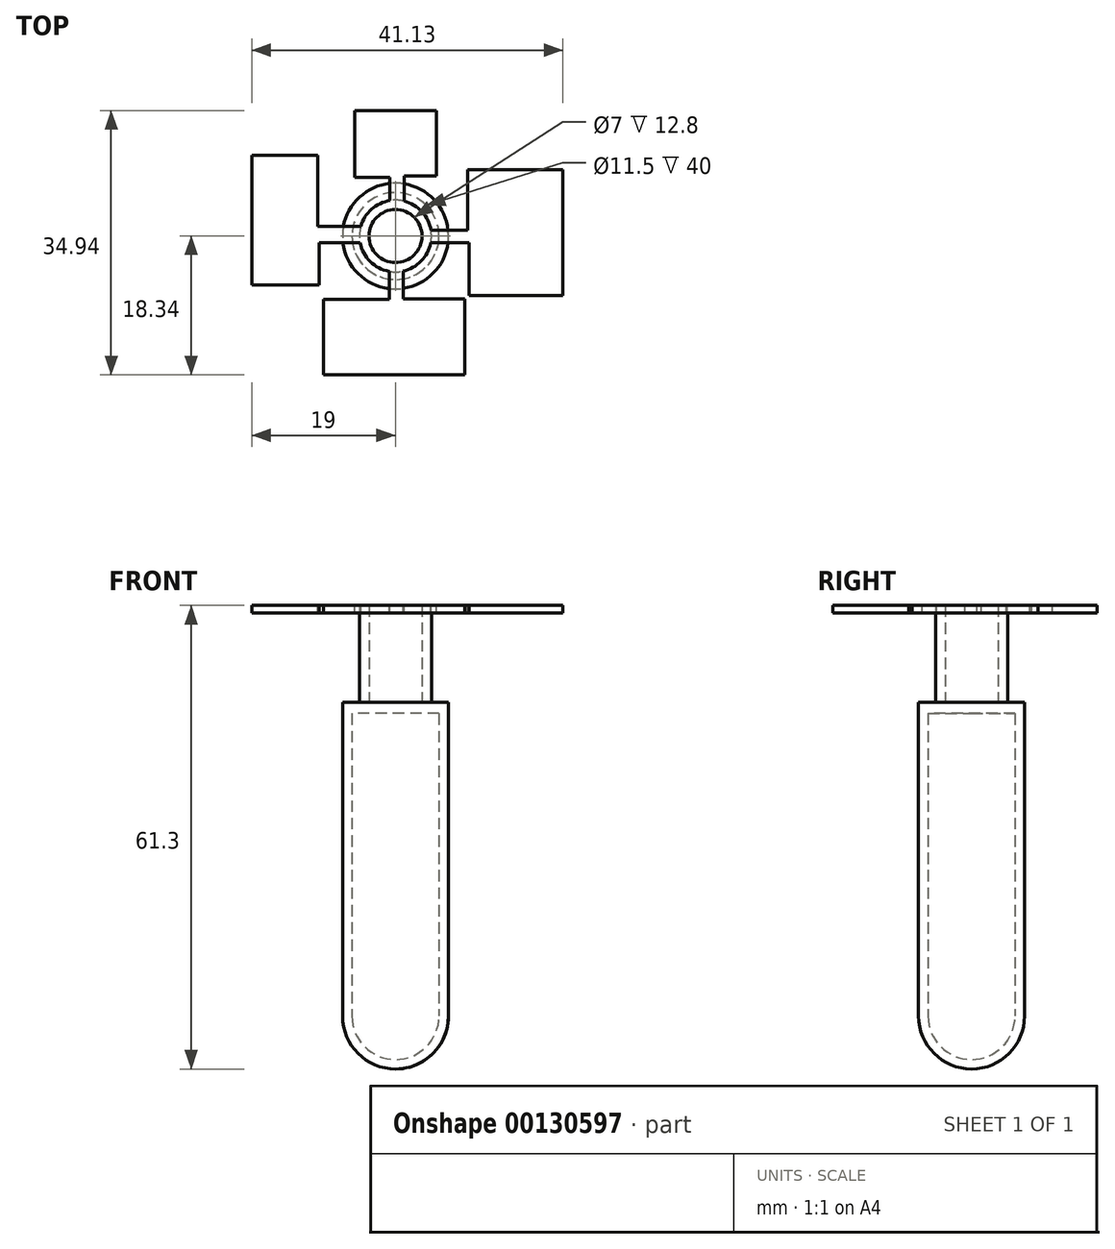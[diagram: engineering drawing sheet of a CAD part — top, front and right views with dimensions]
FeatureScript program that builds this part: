
annotation { "Feature Type Name" : "Feature", "Feature Type Description" : "" }
export const myFeature = defineFeature(function(context is Context, id is Id, definition is map)
    precondition{}
    {
        {
            var Q0;
            Q0=qCreatedBy(makeId("Top.planeOp"),FACE);
            var sketch = newSketch(context, id + "F0", { "sketchPlane" : qUnion([Q0])});
            skCircle(sketch, "E0", {"center": v(0, 0) * mm, "radius": 7 * mm});
            skSolve(sketch);
        }
        {
            var Q0;
            Q0=makeQuery(id+"F0.imprint","IMPRINT",FACE,{"disambiguationData":[TD([[makeQuery(id+"F0.imprint","IMPRINT",EDGE,{"derivedFrom":sQuery(id+"F0.wireOp",EDGE,"E0")}),1.0]])]});
            extrude(context, id + "F1", {"entities" : qUnion([Q0]), "oppositeDirection" : true, "depth" : 7 * mm});
        }
        {
            var Q0;
            Q0=makeQuery(id+"F1.opExtrude","CAP_EDGE",EDGE,{"disambiguationData":[OSD([sQuery(id+"F0.wireOp",EDGE,"E0")])],"isStart":false});
            fillet(context, id + "F2", {"entities" : qUnion([Q0]), "radius" : 7 * mm, "tangentPropagation" : true, "allowEdgeOverflow" : false});
        }
        {
            var Q0;
            Q0=makeQuery(id+"F1.opExtrude","CAP_FACE",FACE,{"disambiguationData":[OSD([sQuery(id+"F0.wireOp",EDGE,"E0")])],"isStart":true});
            var sketch = newSketch(context, id + "F3", { "sketchPlane" : qUnion([Q0])});
            skCircle(sketch, "E1", {"center": v(0, 0) * mm, "radius": 5.75 * mm});
            skLineSegment(sketch, "E2", {"start": v(-5.75, 0) * mm, "end": v(5.75, 0) * mm});
            skSolve(sketch);
        }
        {
            var Q0;
            {var subQ0=sQuery(id+"F3.wireOp",EDGE,"E2");Q0=makeQuery(id+"F3.imprint","IMPRINT",FACE,{"disambiguationData":[TD([[makeQuery(id+"F3.imprint","IMPRINT",EDGE,{"derivedFrom":subQ0}),1.0]])]});}
            var Q1;
            Q1=sQuery(id+"F3.wireOp",EDGE,"E2");
            revolve(context, id + "F4", {"operationType" : NewBodyOperationType.REMOVE, "entities" : qUnion([Q0]), "axis" : qUnion([Q1]), "revolveType" : RevolveType.FULL, "oppositeDirection" : true});
        }
        {
            var Q0;
            Q0=makeQuery(id+"F1.opExtrude","CAP_FACE",FACE,{"disambiguationData":[OSD([sQuery(id+"F0.wireOp",EDGE,"E0")])],"isStart":true});
            extrude(context, id + "F5", {"entities" : qUnion([Q0]), "operationType" : NewBodyOperationType.ADD, "depth" : 40 * mm, "offsetDistance" : 25 * mm});
        }
        {
            var Q0;
            Q0=makeQuery(id+"F5.opExtrude","CAP_FACE",FACE,{"disambiguationData":[OSD([sQuery(id+"F0.wireOp",EDGE,"E0")])],"isStart":false});
            var sketch = newSketch(context, id + "F6", { "sketchPlane" : qUnion([Q0])});
            skCircle(sketch, "E3", {"center": v(0, 0) * mm, "radius": 5.75 * mm});
            skSolve(sketch);
        }
        {
            var Q0;
            Q0=makeQuery(id+"F6.imprint","IMPRINT",FACE,{"disambiguationData":[TD([[makeQuery(id+"F6.imprint","IMPRINT",EDGE,{"derivedFrom":sQuery(id+"F6.wireOp",EDGE,"E3")}),-1.0]])]});
            var Q1;
            Q1=makeQuery(id+"F6.imprint","IMPRINT",FACE,{"disambiguationData":[TD([[makeQuery(id+"F6.imprint","IMPRINT",EDGE,{"derivedFrom":sQuery(id+"F6.wireOp",EDGE,"E3")}),1.0]])]});
            extrude(context, id + "F7", {"entities" : qUnion([Q0, Q1]), "operationType" : NewBodyOperationType.ADD, "depth" : 1.5 * mm});
        }
        {
            var Q0;
            Q0=makeQuery(id+"F7.opExtrude","CAP_FACE",FACE,{"disambiguationData":[OSD([sQuery(id+"F0.wireOp",EDGE,"E0")])],"isStart":false});
            var sketch = newSketch(context, id + "F8", { "sketchPlane" : qUnion([Q0])});
            skCircle(sketch, "E4", {"center": v(0, 0) * mm, "radius": 3.5 * mm});
            skCircle(sketch, "E5", {"center": v(0, 0) * mm, "radius": 4.75 * mm});
            skSolve(sketch);
        }
        {
            var Q0;
            Q0=makeQuery(id+"F8.imprint","IMPRINT",FACE,{"disambiguationData":[TD([[makeQuery(id+"F8.imprint","IMPRINT",EDGE,{"derivedFrom":sQuery(id+"F8.wireOp",EDGE,"E4")}),-1.0]])]});
            extrude(context, id + "F9", {"entities" : qUnion([Q0]), "operationType" : NewBodyOperationType.ADD, "depth" : 12.8 * mm});
        }
        {
            var Q0;
            Q0=makeQuery(id+"F9.opExtrude","CAP_FACE",FACE,{"disambiguationData":[OSD([sQuery(id+"F8.wireOp",EDGE,"E4"),sQuery(id+"F8.wireOp",EDGE,"E5")])],"isStart":false});
            var sketch = newSketch(context, id + "F10", { "sketchPlane" : qUnion([Q0])});
            skLineSegment(sketch, "E6", {"start": v(-0.72, 4.7) * mm, "end": v(-0.72, 7.73) * mm});
            skLineSegment(sketch, "E7", {"start": v(-0.72, 7.73) * mm, "end": v(-5.36, 7.73) * mm});
            skLineSegment(sketch, "E8", {"start": v(-5.36, 7.73) * mm, "end": v(-5.36, 16.6) * mm});
            skLineSegment(sketch, "E9", {"start": v(-5.36, 16.6) * mm, "end": v(5.42, 16.6) * mm});
            skLineSegment(sketch, "E10", {"start": v(5.42, 16.6) * mm, "end": v(5.42, 7.94) * mm});
            skLineSegment(sketch, "E11", {"start": v(5.42, 7.94) * mm, "end": v(1.13, 7.94) * mm});
            skLineSegment(sketch, "E12", {"start": v(1.13, 7.94) * mm, "end": v(1.13, 4.61) * mm});
            skLineSegment(sketch, "E13", {"start": v(-4.58, 1.26) * mm, "end": v(-10.25, 1.26) * mm});
            skLineSegment(sketch, "E14", {"start": v(-10.25, 1.26) * mm, "end": v(-10.25, 10.68) * mm});
            skLineSegment(sketch, "E15", {"start": v(-10.25, 10.68) * mm, "end": v(-19, 10.68) * mm});
            skLineSegment(sketch, "E16", {"start": v(-19, 10.68) * mm, "end": v(-19, -6.5) * mm});
            skLineSegment(sketch, "E17", {"start": v(-19, -6.5) * mm, "end": v(-10.08, -6.5) * mm});
            skLineSegment(sketch, "E18", {"start": v(-10.08, -6.5) * mm, "end": v(-10.08, -0.88) * mm});
            skLineSegment(sketch, "E19", {"start": v(-10.08, -0.88) * mm, "end": v(-4.67, -0.88) * mm});
            skLineSegment(sketch, "E20", {"start": v(-0.84, -4.67) * mm, "end": v(-0.84, -8.35) * mm});
            skLineSegment(sketch, "E21", {"start": v(-0.84, -8.35) * mm, "end": v(-9.48, -8.35) * mm});
            skLineSegment(sketch, "E22", {"start": v(-9.48, -8.35) * mm, "end": v(-9.48, -18.34) * mm});
            skLineSegment(sketch, "E23", {"start": v(-9.48, -18.34) * mm, "end": v(9.17, -18.34) * mm});
            skLineSegment(sketch, "E24", {"start": v(9.17, -18.34) * mm, "end": v(9.17, -8.32) * mm});
            skLineSegment(sketch, "E25", {"start": v(9.17, -8.32) * mm, "end": v(1.01, -8.32) * mm});
            skLineSegment(sketch, "E26", {"start": v(1.01, -8.32) * mm, "end": v(1.01, -4.64) * mm});
            skLineSegment(sketch, "E27", {"start": v(4.7, 0.74) * mm, "end": v(9.54, 0.74) * mm});
            skLineSegment(sketch, "E28", {"start": v(9.54, 0.74) * mm, "end": v(9.54, 8.77) * mm});
            skLineSegment(sketch, "E29", {"start": v(9.54, 8.77) * mm, "end": v(22.13, 8.77) * mm});
            skLineSegment(sketch, "E30", {"start": v(22.13, 8.77) * mm, "end": v(22.13, -5.64) * mm});
            skLineSegment(sketch, "E31", {"start": v(22.13, -5.64) * mm, "end": v(22.13, -7.86) * mm});
            skLineSegment(sketch, "E32", {"start": v(22.13, -7.86) * mm, "end": v(9.7, -7.86) * mm});
            skLineSegment(sketch, "E33", {"start": v(9.7, -7.86) * mm, "end": v(9.7, -0.9) * mm});
            skLineSegment(sketch, "E34", {"start": v(9.7, -0.9) * mm, "end": v(4.66, -0.9) * mm});
            skSolve(sketch);
        }
        {
            var Q0;
            {var subQ0=sQuery(id+"F10.wireOp",EDGE,"E13");Q0=makeQuery(id+"F10.imprint","IMPRINT",FACE,{"disambiguationData":[TD([[makeQuery(id+"F10.imprint","IMPRINT",EDGE,{"derivedFrom":subQ0}),1.0]])]});}
            var Q1;
            {var subQ0=sQuery(id+"F10.wireOp",EDGE,"E6");Q1=makeQuery(id+"F10.imprint","IMPRINT",FACE,{"disambiguationData":[TD([[makeQuery(id+"F10.imprint","IMPRINT",EDGE,{"derivedFrom":subQ0}),-1.0]])]});}
            var Q2;
            {var subQ0=sQuery(id+"F10.wireOp",EDGE,"E27");Q2=makeQuery(id+"F10.imprint","IMPRINT",FACE,{"disambiguationData":[TD([[makeQuery(id+"F10.imprint","IMPRINT",EDGE,{"derivedFrom":subQ0}),-1.0]])]});}
            var Q3;
            {var subQ0=sQuery(id+"F10.wireOp",EDGE,"E20");Q3=makeQuery(id+"F10.imprint","IMPRINT",FACE,{"disambiguationData":[TD([[makeQuery(id+"F10.imprint","IMPRINT",EDGE,{"derivedFrom":subQ0}),1.0]])]});}
            extrude(context, id + "F11", {"entities" : qUnion([Q0, Q1, Q2, Q3]), "operationType" : NewBodyOperationType.ADD, "oppositeDirection" : true, "depth" : 1 * mm});
        }
    });
